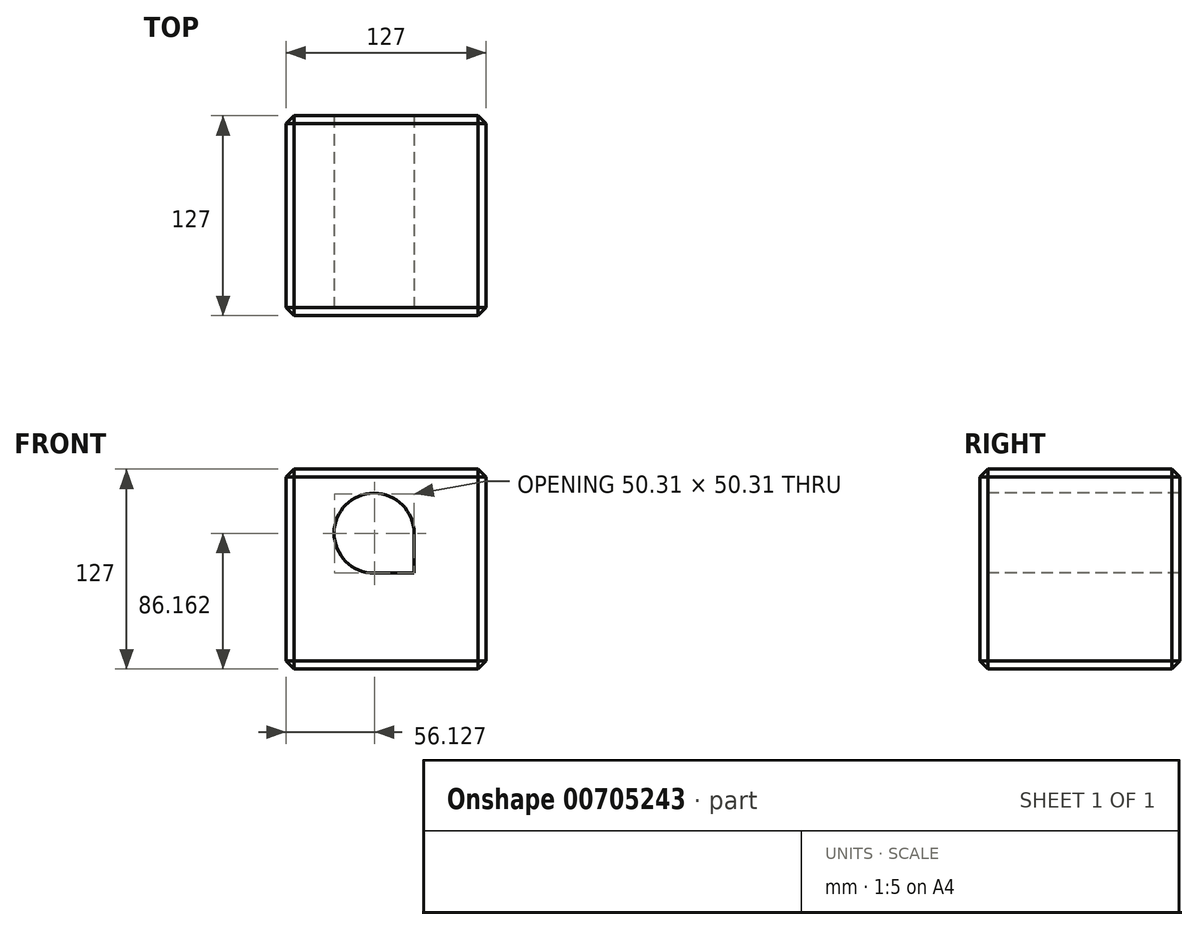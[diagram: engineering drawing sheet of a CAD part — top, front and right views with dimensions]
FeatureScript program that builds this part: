
annotation { "Feature Type Name" : "Feature", "Feature Type Description" : "" }
export const myFeature = defineFeature(function(context is Context, id is Id, definition is map)
    precondition{}
    {
        {
            var Q0;
            Q0=qCreatedBy(makeId("Front.planeOp"),FACE);
            var sketch = newSketch(context, id + "F0", { "sketchPlane" : qUnion([Q0])});
            skLineSegment(sketch, "E0", {"start": v(-63.73, 77.19) * mm, "end": v(63.27, 77.19) * mm});
            skLineSegment(sketch, "E1", {"start": v(63.27, 77.19) * mm, "end": v(63.27, -49.81) * mm});
            skLineSegment(sketch, "E2", {"start": v(63.27, -49.81) * mm, "end": v(-63.73, -49.81) * mm});
            skLineSegment(sketch, "E3", {"start": v(-63.73, -49.81) * mm, "end": v(-63.73, 77.19) * mm});
            skSolve(sketch);
        }
        {
            var Q0;
            Q0=makeQuery(id+"F0.imprint","IMPRINT",FACE,{"disambiguationData":[TD([[makeQuery(id+"F0.imprint","IMPRINT",EDGE,{"derivedFrom":sQuery(id+"F0.wireOp",EDGE,"E0")}),-1.0]])]});
            extrude(context, id + "F1", {"entities" : qUnion([Q0]), "depth" : 127 * mm, "offsetDistance" : 25.4 * mm});
        }
        {
            var Q0;
            Q0=makeQuery(id+"F1.opExtrude","CAP_EDGE",EDGE,{"disambiguationData":[OSD([sQuery(id+"F0.wireOp",EDGE,"E0")])],"isStart":false});
            var Q1;
            Q1=makeQuery(id+"F1.opExtrude","SWEPT_EDGE",EDGE,{"disambiguationData":[OSD([sQuery(id+"F0.wireOp",EDGE,"E0"),sQuery(id+"F0.wireOp",EDGE,"E1")])]});
            var Q2;
            Q2=makeQuery(id+"F1.opExtrude","SWEPT_EDGE",EDGE,{"disambiguationData":[OSD([sQuery(id+"F0.wireOp",EDGE,"E1"),sQuery(id+"F0.wireOp",EDGE,"E2")])]});
            var Q3;
            Q3=makeQuery(id+"F1.opExtrude","CAP_EDGE",EDGE,{"disambiguationData":[OSD([sQuery(id+"F0.wireOp",EDGE,"E2")])],"isStart":false});
            var Q4;
            Q4=makeQuery(id+"F1.opExtrude","SWEPT_EDGE",EDGE,{"disambiguationData":[OSD([sQuery(id+"F0.wireOp",EDGE,"E2"),sQuery(id+"F0.wireOp",EDGE,"E3")])]});
            var Q5;
            Q5=makeQuery(id+"F1.opExtrude","CAP_EDGE",EDGE,{"disambiguationData":[OSD([sQuery(id+"F0.wireOp",EDGE,"E2")])],"isStart":true});
            var Q6;
            Q6=makeQuery(id+"F1.opExtrude","SWEPT_FACE",FACE,{"disambiguationData":[OSD([sQuery(id+"F0.wireOp",EDGE,"E0")])]});
            var Q7;
            Q7=makeQuery(id+"F1.opExtrude","CAP_EDGE",EDGE,{"disambiguationData":[OSD([sQuery(id+"F0.wireOp",EDGE,"E3")])],"isStart":true});
            var Q8;
            Q8=makeQuery(id+"F1.opExtrude","CAP_EDGE",EDGE,{"disambiguationData":[OSD([sQuery(id+"F0.wireOp",EDGE,"E1")])],"isStart":true});
            var Q9;
            Q9=makeQuery(id+"F1.opExtrude","CAP_EDGE",EDGE,{"disambiguationData":[OSD([sQuery(id+"F0.wireOp",EDGE,"E3")])],"isStart":false});
            var Q10;
            Q10=makeQuery(id+"F1.opExtrude","CAP_EDGE",EDGE,{"disambiguationData":[OSD([sQuery(id+"F0.wireOp",EDGE,"E1")])],"isStart":false});
            chamfer(context, id + "F2", {"entities" : qUnion([Q0, Q1, Q2, Q3, Q4, Q5, Q6, Q7, Q8, Q9, Q10]), "width" : 5.08 * mm, "tangentPropagation" : true});
        }
        {
            var Q0;
            Q0=makeQuery(id+"F1.opExtrude","CAP_FACE",FACE,{"disambiguationData":[OSD([sQuery(id+"F0.wireOp",EDGE,"E0"),sQuery(id+"F0.wireOp",EDGE,"E1"),sQuery(id+"F0.wireOp",EDGE,"E2"),sQuery(id+"F0.wireOp",EDGE,"E3")])],"isStart":false});
            var sketch = newSketch(context, id + "F3", { "sketchPlane" : qUnion([Q0])});
            skArc(sketch, "E4", {"start": v(17.55, 36.6) * mm, "mid": v(-25.8, 54.56) * mm, "end": v(-7.85, 11.2) * mm});
            skLineSegment(sketch, "E5", {"start": v(-7.85, 11.2) * mm, "end": v(17.55, 11.2) * mm});
            skLineSegment(sketch, "E6", {"start": v(17.55, 36.6) * mm, "end": v(17.55, 11.2) * mm});
            skSolve(sketch);
        }
        {
            var Q0;
            Q0=makeQuery(id+"F3.imprint","IMPRINT",FACE,{"disambiguationData":[TD([[makeQuery(id+"F3.imprint","IMPRINT",EDGE,{"derivedFrom":sQuery(id+"F3.wireOp",EDGE,"E4")}),1.0]])]});
            extrude(context, id + "F4", {"entities" : qUnion([Q0]), "operationType" : NewBodyOperationType.REMOVE, "oppositeDirection" : true, "depth" : 127 * mm, "offsetDistance" : 25.4 * mm});
        }
    });
